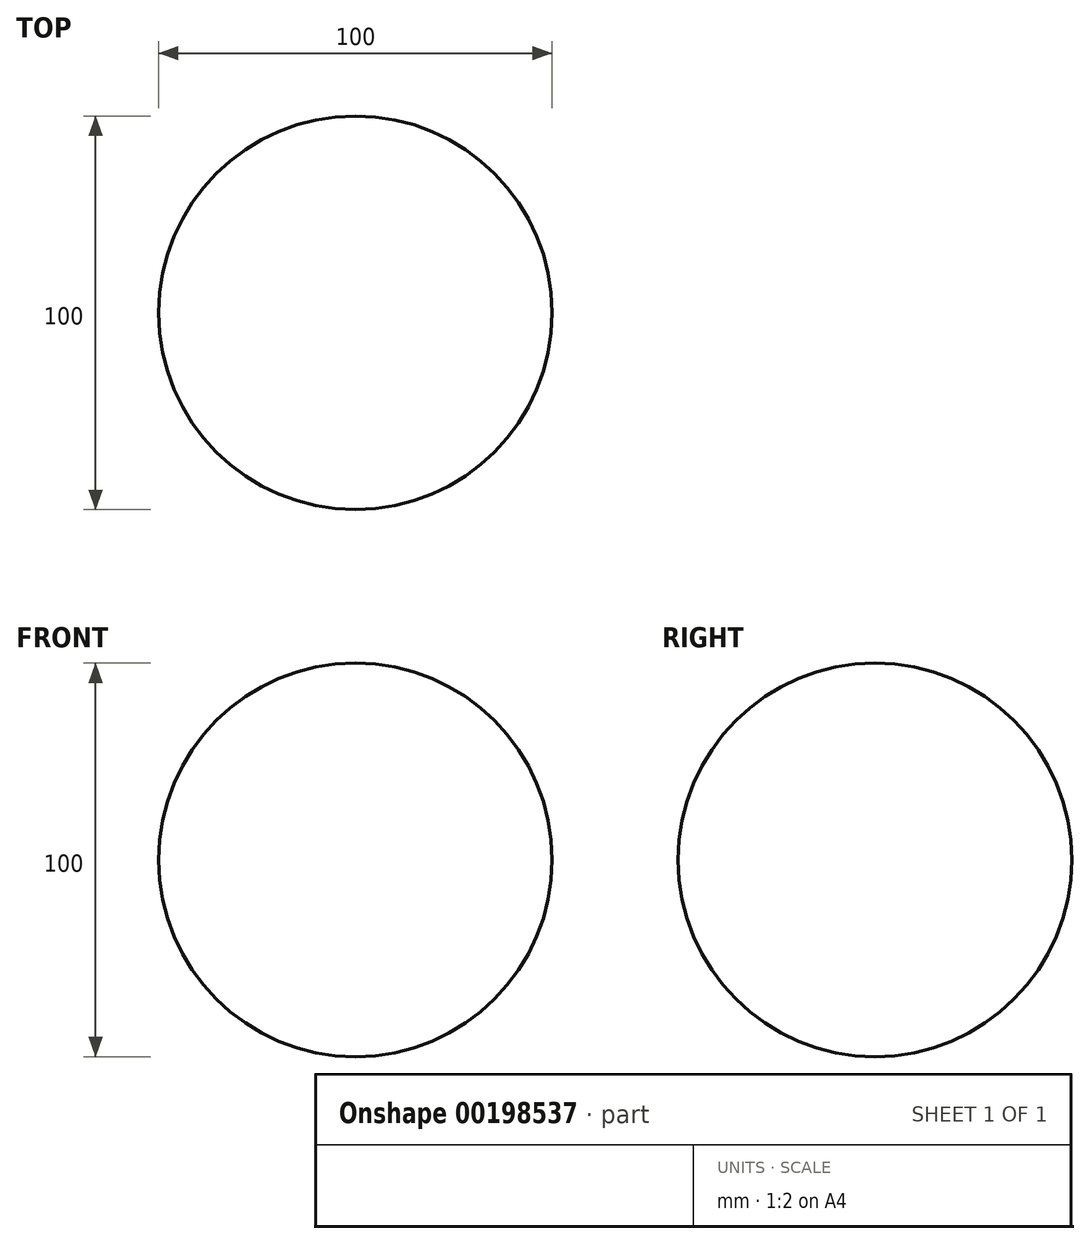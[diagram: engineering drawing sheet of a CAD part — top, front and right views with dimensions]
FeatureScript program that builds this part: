
annotation { "Feature Type Name" : "Feature", "Feature Type Description" : "" }
export const myFeature = defineFeature(function(context is Context, id is Id, definition is map)
    precondition{}
    {
        {
            var Q0;
            Q0=qCreatedBy(makeId("Top.planeOp"),FACE);
            var sketch = newSketch(context, id + "F0", { "sketchPlane" : qUnion([Q0])});
            skArc(sketch, "E0", {"start": v(0, 50) * mm, "mid": v(-50, 0) * mm, "end": v(0, -50) * mm});
            skLineSegment(sketch, "E1", {"start": v(0, 50) * mm, "end": v(0, -50) * mm, "construction": true});
            skSolve(sketch);
        }
        {
            var Q0;
            Q0=sQuery(id+"F0.wireOp",EDGE,"E0");
            var Q1;
            Q1=sQuery(id+"F0.wireOp",EDGE,"E1");
            revolve(context, id + "F1", {"bodyType" : ToolBodyType.SURFACE, "surfaceEntities" : qUnion([Q0]), "axis" : qUnion([Q1]), "revolveType" : RevolveType.FULL});
        }
    });
